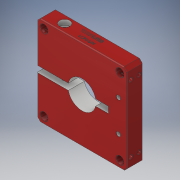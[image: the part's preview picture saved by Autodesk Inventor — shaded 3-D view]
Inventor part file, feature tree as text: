
AUTODESK INVENTOR PART (.ipt)
format: ipt  version: 2017 (Build 210142000, 142)  size: 1,032,192 bytes
history: native  units: mm
features: hole x4, sketch x3, extrude x1, projected_geometry x1, other x1
ambient origin geometry x8: Origin, YZ Plane, XZ Plane, XY Plane, X Axis, Y Axis, Z Axis, Center Point
bodies: Solid1 (feature_tree)
feature tree (10):
  sketch  "Sketch1"  dims[d0=22.1mm d1=42.0mm]
  sketch  "Sketch2"  dims[d2=71.12mm d3=5.0mm]
  hole  "M4 hole"  [1 undecoded]
  hole  "M4 ClearanceHole"  [1 undecoded]
  hole  "M4 bolt head hole"  [1 undecoded]
  extrude  "Cutout"  Depth=2.0mm
  hole  "M4 holes"  [1 undecoded]
  projected_geometry  "Projected Loop1"
  sketch  "Sketch3"  dims[d7=3.3mm d8=6.0mm d9=4.0mm d10=2.0mm d11=90.0deg d12=8.0mm d13=20.594885mm d14=4.2mm d15=6.0mm d16=4.0mm d17=2.0mm d18=90.0deg d19=35.0mm d20=0.0mm d21=8.0mm d22=6.0mm d23=4.0mm d24=2.0mm d25=90.0deg d26=4.0mm d27=0.0mm d28=10.0mm d29=0.0mm d30=12.5mm d31=6.0mm d32=3.3mm d33=6.0mm d34=4.0mm d35=2.0mm d36=90.0deg d37=8.0mm d38=20.594885mm d39=20.0mm]
  other  "13108-001-1-solid1"
note: 4 required parameter values undecoded (feature->parameter linkage not recoverable at this tier; creation-order binding heuristic only, values carry confidence <= 0.55)
